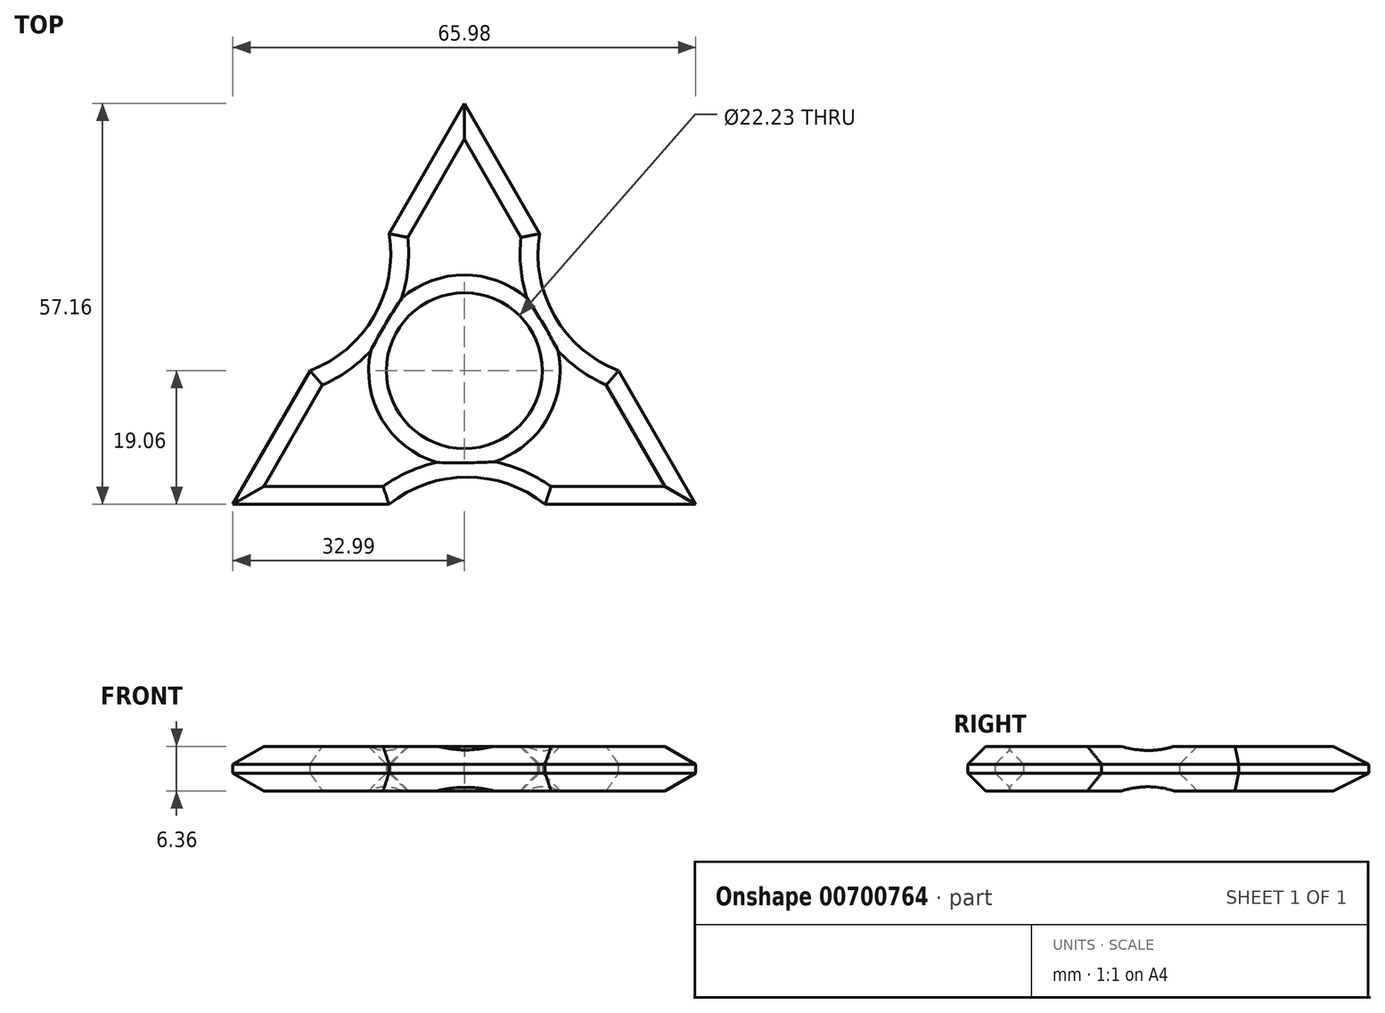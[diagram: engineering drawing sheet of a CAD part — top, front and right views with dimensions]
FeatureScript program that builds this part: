
annotation { "Feature Type Name" : "Feature", "Feature Type Description" : "" }
export const myFeature = defineFeature(function(context is Context, id is Id, definition is map)
    precondition{}
    {
        {
            var Q0;
            Q0=qCreatedBy(makeId("Top.planeOp"),FACE);
            var sketch = newSketch(context, id + "F0", { "sketchPlane" : qUnion([Q0])});
            skCircle(sketch, "E0", {"center": v(0, 0) * mm, "radius": 38.1 * mm});
            skCircle(sketch, "E1", {"center": v(0, 0) * mm, "radius": 11.11 * mm});
            skSolve(sketch);
        }
        {
            var Q0;
            Q0=qSketchRegion(id+"F0",true);
            extrude(context, id + "F1", {"entities" : qUnion([Q0]), "depth" : 3.17 * mm, "offsetDistance" : 25.4 * mm, "hasSecondDirection" : true, "secondDirectionOppositeDirection" : true, "secondDirectionDepth" : 3.17 * mm});
        }
        {
            var Q0;
            Q0=makeQuery(id+"F1.opExtrude","CAP_FACE",FACE,{"disambiguationData":[OSD([sQuery(id+"F0.wireOp",EDGE,"E0"),sQuery(id+"F0.wireOp",EDGE,"E1")])],"isStart":false});
            var sketch = newSketch(context, id + "F2", { "sketchPlane" : qUnion([Q0])});
            skLineSegment(sketch, "E2", {"start": v(0, 38.1) * mm, "end": v(-32.99, -19.06) * mm});
            skLineSegment(sketch, "E3", {"start": v(-32.99, -19.06) * mm, "end": v(32.99, -19.06) * mm});
            skLineSegment(sketch, "E4", {"start": v(32.99, -19.06) * mm, "end": v(0, 38.1) * mm});
            skSolve(sketch);
        }
        {
            var Q0;
            {var subQ0=sQuery(id+"F2.wireOp",EDGE,"E2");Q0=makeQuery(id+"F2.imprint","IMPRINT",FACE,{"disambiguationData":[TD([[makeQuery(id+"F2.imprint","IMPRINT",EDGE,{"derivedFrom":subQ0}),-1.0]])]});}
            var Q1;
            {var subQ0=sQuery(id+"F2.wireOp",EDGE,"E3");Q1=makeQuery(id+"F2.imprint","IMPRINT",FACE,{"disambiguationData":[TD([[makeQuery(id+"F2.imprint","IMPRINT",EDGE,{"derivedFrom":subQ0}),-1.0]])]});}
            var Q2;
            {var subQ0=sQuery(id+"F2.wireOp",EDGE,"E4");Q2=makeQuery(id+"F2.imprint","IMPRINT",FACE,{"disambiguationData":[TD([[makeQuery(id+"F2.imprint","IMPRINT",EDGE,{"derivedFrom":subQ0}),-1.0]])]});}
            extrude(context, id + "F3", {"entities" : qUnion([Q0, Q1, Q2]), "operationType" : NewBodyOperationType.REMOVE, "oppositeDirection" : true, "depth" : 25.4 * mm, "offsetDistance" : 25.4 * mm});
        }
        {
            var Q0;
            Q0=makeQuery(id+"F1.opExtrude","CAP_FACE",FACE,{"disambiguationData":[OSD([sQuery(id+"F0.wireOp",EDGE,"E0"),sQuery(id+"F0.wireOp",EDGE,"E1")])],"isStart":false});
            var sketch = newSketch(context, id + "F4", { "sketchPlane" : qUnion([Q0])});
            skArc(sketch, "E5", {"start": v(-21.99, 0) * mm, "mid": v(-12.87, 7.75) * mm, "end": v(-10.72, 19.52) * mm});
            skArc(sketch, "E6", {"start": v(10.72, 19.52) * mm, "mid": v(12.87, 7.75) * mm, "end": v(21.99, 0) * mm});
            skPoint(sketch, "E7.endSnap0", {"position": v(0, -19.06) * mm});
            skArc(sketch, "E8", {"start": v(11.5, -19.06) * mm, "mid": v(0.39, -15.16) * mm, "end": v(-10.72, -19.06) * mm});
            skSolve(sketch);
        }
        {
            var Q0;
            Q0=qSketchRegion(id+"F4",true);
            var Q1;
            {var subQ0=sQuery(id+"F4.wireOp",EDGE,"E5");Q1=makeQuery(id+"F4.imprint","IMPRINT",FACE,{"disambiguationData":[TD([[makeQuery(id+"F4.imprint","IMPRINT",EDGE,{"derivedFrom":subQ0}),1.0]])]});}
            var Q2;
            {var subQ0=sQuery(id+"F4.wireOp",EDGE,"E6");Q2=makeQuery(id+"F4.imprint","IMPRINT",FACE,{"disambiguationData":[TD([[makeQuery(id+"F4.imprint","IMPRINT",EDGE,{"derivedFrom":subQ0}),1.0]])]});}
            var Q3;
            {var subQ0=sQuery(id+"F4.wireOp",EDGE,"E8");Q3=makeQuery(id+"F4.imprint","IMPRINT",FACE,{"disambiguationData":[TD([[makeQuery(id+"F4.imprint","IMPRINT",EDGE,{"derivedFrom":subQ0}),1.0]])]});}
            extrude(context, id + "F5", {"entities" : qUnion([Q0, Q1, Q2, Q3]), "operationType" : NewBodyOperationType.REMOVE, "oppositeDirection" : true, "depth" : 25.4 * mm, "offsetDistance" : 25.4 * mm});
        }
        {
            var Q0;
            Q0=makeQuery(id+"F1.opExtrude","CAP_FACE",FACE,{"disambiguationData":[OSD([sQuery(id+"F0.wireOp",EDGE,"E0"),sQuery(id+"F0.wireOp",EDGE,"E1")])],"isStart":false});
            var Q1;
            Q1=makeQuery(id+"F1.opExtrude","CAP_FACE",FACE,{"disambiguationData":[OSD([sQuery(id+"F0.wireOp",EDGE,"E0"),sQuery(id+"F0.wireOp",EDGE,"E1")])],"isStart":true});
            chamfer(context, id + "F6", {"entities" : qUnion([Q0, Q1]), "width" : 2.54 * mm, "tangentPropagation" : true});
        }
    });
